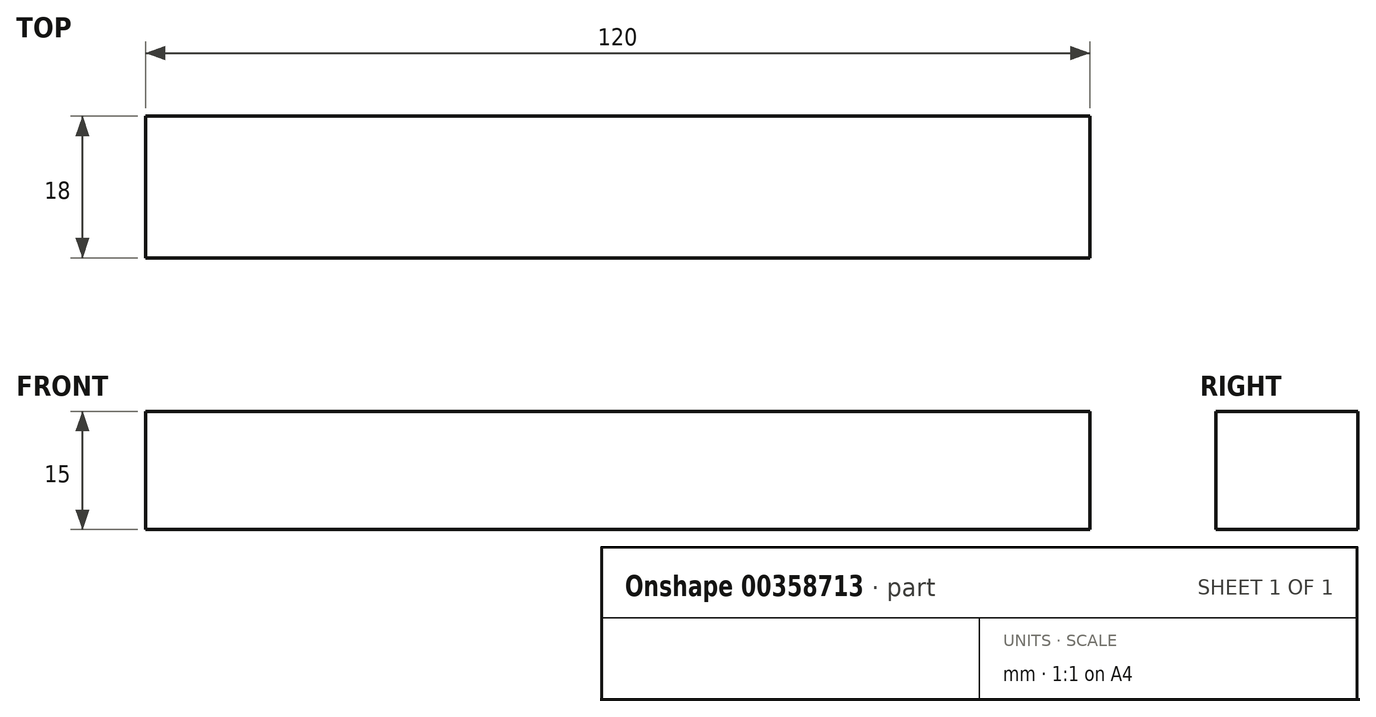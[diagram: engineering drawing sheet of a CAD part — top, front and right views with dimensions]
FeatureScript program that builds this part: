
annotation { "Feature Type Name" : "Feature", "Feature Type Description" : "" }
export const myFeature = defineFeature(function(context is Context, id is Id, definition is map)
    precondition{}
    {
        {
            var Q0;
            Q0=qCreatedBy(makeId("Right.planeOp"),FACE);
            var sketch = newSketch(context, id + "F0", { "sketchPlane" : qUnion([Q0])});
            skLineSegment(sketch, "E0.bottom", {"start": v(9, -7.5) * mm, "end": v(-9, -7.5) * mm});
            skLineSegment(sketch, "E0.top", {"start": v(9, 7.5) * mm, "end": v(-9, 7.5) * mm});
            skLineSegment(sketch, "E0.left", {"start": v(9, -7.5) * mm, "end": v(9, 7.5) * mm});
            skLineSegment(sketch, "E0.right", {"start": v(-9, -7.5) * mm, "end": v(-9, 7.5) * mm});
            skPoint(sketch, "E0.middle", {"position": v(0, 0) * mm});
            skSolve(sketch);
        }
        {
            var Q0;
            Q0=qSketchRegion(id+"F0",true);
            extrude(context, id + "F1", {"entities" : qUnion([Q0]), "depth" : 120 * mm});
        }
    });
